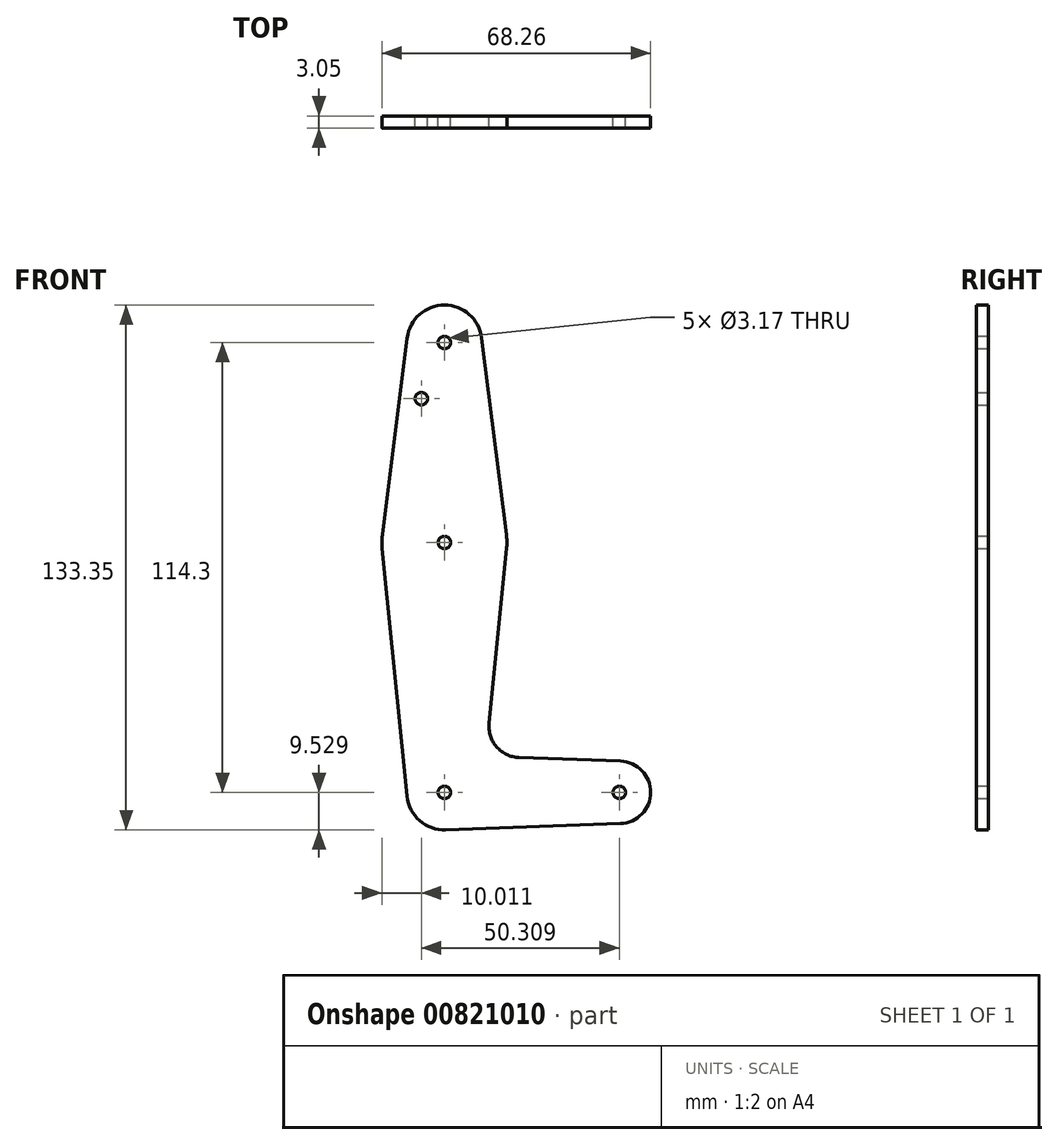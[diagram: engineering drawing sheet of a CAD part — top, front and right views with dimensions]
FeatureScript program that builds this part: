
annotation { "Feature Type Name" : "Feature", "Feature Type Description" : "" }
export const myFeature = defineFeature(function(context is Context, id is Id, definition is map)
    precondition{}
    {
        {
            var Q0;
            Q0=qCreatedBy(makeId("Front.planeOp"),FACE);
            var sketch = newSketch(context, id + "F0", { "sketchPlane" : qUnion([Q0])});
            skLineSegment(sketch, "E0", {"start": v(0, 31.15) * mm, "end": v(0, -83.15) * mm});
            skCircle(sketch, "E1", {"center": v(0, 31.15) * mm, "radius": 9.53 * mm});
            skCircle(sketch, "E2", {"center": v(0, -19.65) * mm, "radius": 15.88 * mm});
            skCircle(sketch, "E3", {"center": v(0, -83.15) * mm, "radius": 9.53 * mm});
            skLineSegment(sketch, "E4", {"start": v(0, -83.15) * mm, "end": v(44.45, -83.15) * mm});
            skLineSegment(sketch, "E5", {"start": v(-9.45, 32.34) * mm, "end": v(-15.85, -18.48) * mm});
            skLineSegment(sketch, "E6", {"start": v(-15.84, -20.8) * mm, "end": v(-9.48, -84.1) * mm});
            skLineSegment(sketch, "E7", {"start": v(9.45, 32.34) * mm, "end": v(15.8, -18.05) * mm});
            skLineSegment(sketch, "E8", {"start": v(0, -92.68) * mm, "end": v(45.5, -91.06) * mm});
            skLineSegment(sketch, "E9", {"start": v(45.43, -75.24) * mm, "end": v(18.97, -74.3) * mm});
            skCircle(sketch, "E10", {"center": v(0, 31.15) * mm, "radius": 1.59 * mm});
            skCircle(sketch, "E11", {"center": v(0, -19.65) * mm, "radius": 1.59 * mm});
            skCircle(sketch, "E12", {"center": v(0, -83.15) * mm, "radius": 1.59 * mm});
            skCircle(sketch, "E13", {"center": v(44.45, -83.15) * mm, "radius": 7.94 * mm});
            skLineSegment(sketch, "E14", {"start": v(16, -19.3) * mm, "end": v(11.34, -65.56) * mm});
            skCircle(sketch, "E15", {"center": v(44.45, -83.15) * mm, "radius": 1.59 * mm});
            skCircle(sketch, "E16", {"center": v(-5.86, 16.87) * mm, "radius": 1.59 * mm});
            skArc(sketch, "E17.filletArc", {"start": v(11.34, -65.56) * mm, "mid": v(13.26, -71.58) * mm, "end": v(18.97, -74.3) * mm});
            skSolve(sketch);
        }
        {
            var Q0;
            {var subQ0=sQuery(id+"F0.wireOp",EDGE,"E2");var subQ2=sQuery(id+"F0.wireOp",EDGE,"E0");var subQ3=makeQuery(id+"F0.imprint","INTERSECT",VERTEX,{"disambiguationData":[OD(1.0)],"derivedFrom":[subQ2,subQ0]});Q0=makeQuery(id+"F0.imprint","IMPRINT",FACE,{"disambiguationData":[TD([[makeQuery(id+"F0.imprint","IMPRINT",EDGE,{"disambiguationData":[TD([[subQ3,-1.0]])],"derivedFrom":subQ2}),1.0]])]});}
            var Q1;
            {var subQ0=sQuery(id+"F0.wireOp",EDGE,"E2");var subQ2=sQuery(id+"F0.wireOp",EDGE,"E0");var subQ4=makeQuery(id+"F0.imprint","INTERSECT",VERTEX,{"disambiguationData":[OD(1.0)],"derivedFrom":[subQ2,subQ0]});Q1=makeQuery(id+"F0.imprint","IMPRINT",FACE,{"disambiguationData":[TD([[makeQuery(id+"F0.imprint","IMPRINT",EDGE,{"disambiguationData":[TD([[subQ4,-1.0]])],"derivedFrom":subQ2}),-1.0]])]});}
            var Q2;
            {var subQ11=sQuery(id+"F0.wireOp",EDGE,"E17.filletArc");Q2=makeQuery(id+"F0.imprint","IMPRINT",FACE,{"disambiguationData":[TD([[makeQuery(id+"F0.imprint","IMPRINT",EDGE,{"derivedFrom":subQ11}),-1.0]])]});}
            var Q3;
            {var subQ0=sQuery(id+"F0.wireOp",EDGE,"E8");var subQ1=sQuery(id+"F0.wireOp",EDGE,"E3");var subQ2=makeQuery(id+"F0.imprint","INTERSECT",VERTEX,{"derivedFrom":[subQ1,subQ0]});Q3=makeQuery(id+"F0.imprint","IMPRINT",FACE,{"disambiguationData":[TD([[makeQuery(id+"F0.imprint","IMPRINT",EDGE,{"disambiguationData":[TD([[subQ2,-1.0]])],"derivedFrom":subQ1}),-1.0]])]});}
            var Q4;
            {var subQ1=sQuery(id+"F0.wireOp",EDGE,"E3");var subQ6=sQuery(id+"F0.wireOp",EDGE,"E0");var subQ7=makeQuery(id+"F0.imprint","INTERSECT",VERTEX,{"derivedFrom":[subQ6,subQ1]});Q4=makeQuery(id+"F0.imprint","IMPRINT",FACE,{"disambiguationData":[TD([[makeQuery(id+"F0.imprint","IMPRINT",EDGE,{"disambiguationData":[TD([[subQ7,-1.0]])],"derivedFrom":subQ6}),-1.0]])]});}
            var Q5;
            {var subQ0=sQuery(id+"F0.wireOp",EDGE,"E3");var subQ1=sQuery(id+"F0.wireOp",EDGE,"E0");var subQ2=makeQuery(id+"F0.imprint","INTERSECT",VERTEX,{"derivedFrom":[subQ1,subQ0]});Q5=makeQuery(id+"F0.imprint","IMPRINT",FACE,{"disambiguationData":[TD([[makeQuery(id+"F0.imprint","IMPRINT",EDGE,{"disambiguationData":[TD([[subQ2,-1.0]])],"derivedFrom":subQ1}),1.0]])]});}
            var Q6;
            Q6=makeQuery(id+"F0.imprint","IMPRINT",FACE,{"disambiguationData":[TD([[makeQuery(id+"F0.imprint","IMPRINT",EDGE,{"derivedFrom":sQuery(id+"F0.wireOp",EDGE,"E15")}),-1.0]])]});
            var Q7;
            Q7=makeQuery(id+"F0.imprint","IMPRINT",FACE,{"disambiguationData":[TD([[makeQuery(id+"F0.imprint","IMPRINT",EDGE,{"derivedFrom":sQuery(id+"F0.wireOp",EDGE,"E10")}),-1.0]])]});
            var Q8;
            Q8=makeQuery(id+"F0.imprint","IMPRINT",FACE,{"disambiguationData":[TD([[makeQuery(id+"F0.imprint","IMPRINT",EDGE,{"derivedFrom":sQuery(id+"F0.wireOp",EDGE,"E16")}),-1.0]])]});
            var Q9;
            {var subQ0=sQuery(id+"F0.wireOp",EDGE,"E1");var subQ1=sQuery(id+"F0.wireOp",EDGE,"E0");var subQ2=makeQuery(id+"F0.imprint","INTERSECT",VERTEX,{"derivedFrom":[subQ1,subQ0]});Q9=makeQuery(id+"F0.imprint","IMPRINT",FACE,{"disambiguationData":[TD([[makeQuery(id+"F0.imprint","IMPRINT",EDGE,{"disambiguationData":[TD([[subQ2,-1.0]])],"derivedFrom":subQ1}),1.0]])]});}
            var Q10;
            {var subQ0=sQuery(id+"F0.wireOp",EDGE,"E2");var subQ2=sQuery(id+"F0.wireOp",EDGE,"E0");var subQ7=makeQuery(id+"F0.imprint","INTERSECT",VERTEX,{"disambiguationData":[OD(0.0)],"derivedFrom":[subQ2,subQ0]});Q10=makeQuery(id+"F0.imprint","IMPRINT",FACE,{"disambiguationData":[TD([[makeQuery(id+"F0.imprint","IMPRINT",EDGE,{"disambiguationData":[TD([[subQ7,-1.0]])],"derivedFrom":subQ2}),1.0]])]});}
            var Q11;
            {var subQ0=sQuery(id+"F0.wireOp",EDGE,"E2");var subQ3=sQuery(id+"F0.wireOp",EDGE,"E0");var subQ4=makeQuery(id+"F0.imprint","INTERSECT",VERTEX,{"disambiguationData":[OD(0.0)],"derivedFrom":[subQ3,subQ0]});Q11=makeQuery(id+"F0.imprint","IMPRINT",FACE,{"disambiguationData":[TD([[makeQuery(id+"F0.imprint","IMPRINT",EDGE,{"disambiguationData":[TD([[subQ4,-1.0]])],"derivedFrom":subQ3}),-1.0]])]});}
            extrude(context, id + "F1", {"entities" : qUnion([Q0, Q1, Q2, Q3, Q4, Q5, Q6, Q7, Q8, Q9, Q10, Q11]), "depth" : 3.05 * mm, "offsetDistance" : 25.4 * mm});
        }
    });
